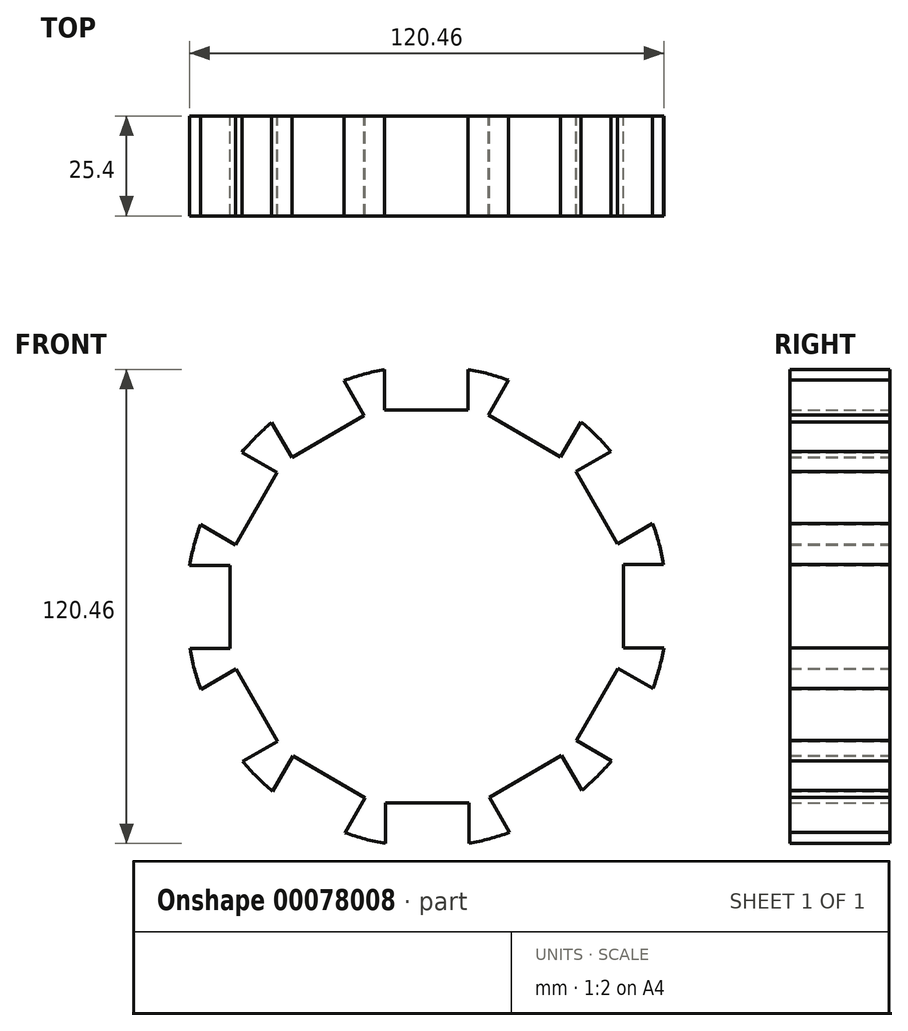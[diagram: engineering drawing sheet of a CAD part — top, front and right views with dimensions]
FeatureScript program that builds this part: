
annotation { "Feature Type Name" : "Feature", "Feature Type Description" : "" }
export const myFeature = defineFeature(function(context is Context, id is Id, definition is map)
    precondition{}
    {
        {
            var Q0;
            Q0=qCreatedBy(makeId("Front.planeOp"),FACE);
            var sketch = newSketch(context, id + "F0", { "sketchPlane" : qUnion([Q0])});
            skCircle(sketch, "E0", {"center": v(0, 0) * mm, "radius": 61.14 * mm});
            skSolve(sketch);
        }
        {
            var Q0;
            Q0=makeQuery(id+"F0.imprint","IMPRINT",FACE,{"disambiguationData":[TD([[makeQuery(id+"F0.imprint","IMPRINT",EDGE,{"derivedFrom":sQuery(id+"F0.wireOp",EDGE,"E0")}),1.0]])]});
            extrude(context, id + "F1", {"entities" : qUnion([Q0]), "depth" : 25.4 * mm});
        }
        {
            var Q0;
            Q0=qCreatedBy(makeId("Front.planeOp"),FACE);
            var sketch = newSketch(context, id + "F2", { "sketchPlane" : qUnion([Q0])});
            skLineSegment(sketch, "E1.bottom", {"start": v(-10.72, 80.64) * mm, "end": v(10.47, 80.64) * mm});
            skLineSegment(sketch, "E1.top", {"start": v(-10.72, 49.93) * mm, "end": v(10.47, 49.93) * mm});
            skLineSegment(sketch, "E1.left", {"start": v(-10.72, 80.64) * mm, "end": v(-10.72, 49.93) * mm});
            skLineSegment(sketch, "E1.right", {"start": v(10.47, 80.64) * mm, "end": v(10.47, 49.93) * mm});
            skSolve(sketch);
        }
        {
            var Q0;
            Q0=makeQuery(id+"F2.imprint","IMPRINT",FACE,{"disambiguationData":[TD([[makeQuery(id+"F2.imprint","IMPRINT",EDGE,{"derivedFrom":sQuery(id+"F2.wireOp",EDGE,"E1.bottom")}),-1.0]])]});
            extrude(context, id + "F3", {"entities" : qUnion([Q0]), "operationType" : NewBodyOperationType.REMOVE, "depth" : 25.4 * mm});
        }
        {
            var Q0;
            Q0=qCreatedBy(makeId("Top.planeOp"),FACE);
            var sketch = newSketch(context, id + "F4", { "sketchPlane" : qUnion([Q0])});
            skLineSegment(sketch, "E2", {"start": v(0, 69.66) * mm, "end": v(0, -53.04) * mm, "construction": true});
            skSolve(sketch);
        }
        {
            var Q0;
            Q0=makeQuery(id+"F3.boolean.opBoolean","COPY",FACE,{"derivedFrom":makeQuery(id+"F3.opExtrude","SWEPT_FACE",FACE,{"disambiguationData":[OSD([sQuery(id+"F2.wireOp",EDGE,"E1.left")])]})});
            var Q1;
            Q1=makeQuery(id+"F3.boolean.opBoolean","COPY",FACE,{"derivedFrom":makeQuery(id+"F3.opExtrude","SWEPT_FACE",FACE,{"disambiguationData":[OSD([sQuery(id+"F2.wireOp",EDGE,"E1.top")])]})});
            var Q2;
            Q2=makeQuery(id+"F3.boolean.opBoolean","COPY",FACE,{"derivedFrom":makeQuery(id+"F3.opExtrude","SWEPT_FACE",FACE,{"disambiguationData":[OSD([sQuery(id+"F2.wireOp",EDGE,"E1.right")])]})});
            var Q3;
            Q3=sQuery(id+"F4.wireOp",EDGE,"E2");
            circularPattern(context, id + "F5", {"faces" : qUnion([Q0, Q1, Q2]), "axis" : qUnion([Q3]), "angle" : 30 * degree, "instanceCount" : 12, "patternType" : PatternType.FACE});
        }
    });
